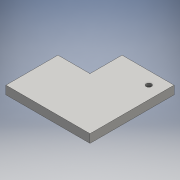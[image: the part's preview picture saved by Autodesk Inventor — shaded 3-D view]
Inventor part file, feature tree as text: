
AUTODESK INVENTOR PART (.ipt)
format: ipt  version: 2016 SP1 (Build 200210100, 210)  size: 115,200 bytes
history: native  units: mm
features: extrude x4, sketch x4
ambient origin geometry x8: Origin, YZ Plane, XZ Plane, XY Plane, X Axis, Y Axis, Z Axis, Center Point
bodies: Solid1 (feature_tree)
feature tree (8):
  extrude  "Extrusion1"  Depth=80.0mm
  extrude  "Extrusion2"  Depth=8.0mm
  extrude  "Extrusion3"  Depth=5.0mm
  extrude  "Extrusion4"  Depth=5.0mm
  sketch  "Sketch1"  dims[d0=80.0mm d1=80.0mm]
  sketch  "Sketch2"  dims[d2=8.0mm d3=0.0mm d4=40.0mm]
  sketch  "Sketch3"  dims[d5=40.0mm d6=5.0mm]
  sketch  "Sketch4"  dims[d7=12.0mm d8=12.0mm d9=8.0mm d10=0.0mm d11=16.0mm d12=5.0mm d13=0.0mm d14=30.5mm d15=30.5mm d16=0.0mm d17=5.0mm d18=0.0mm]
